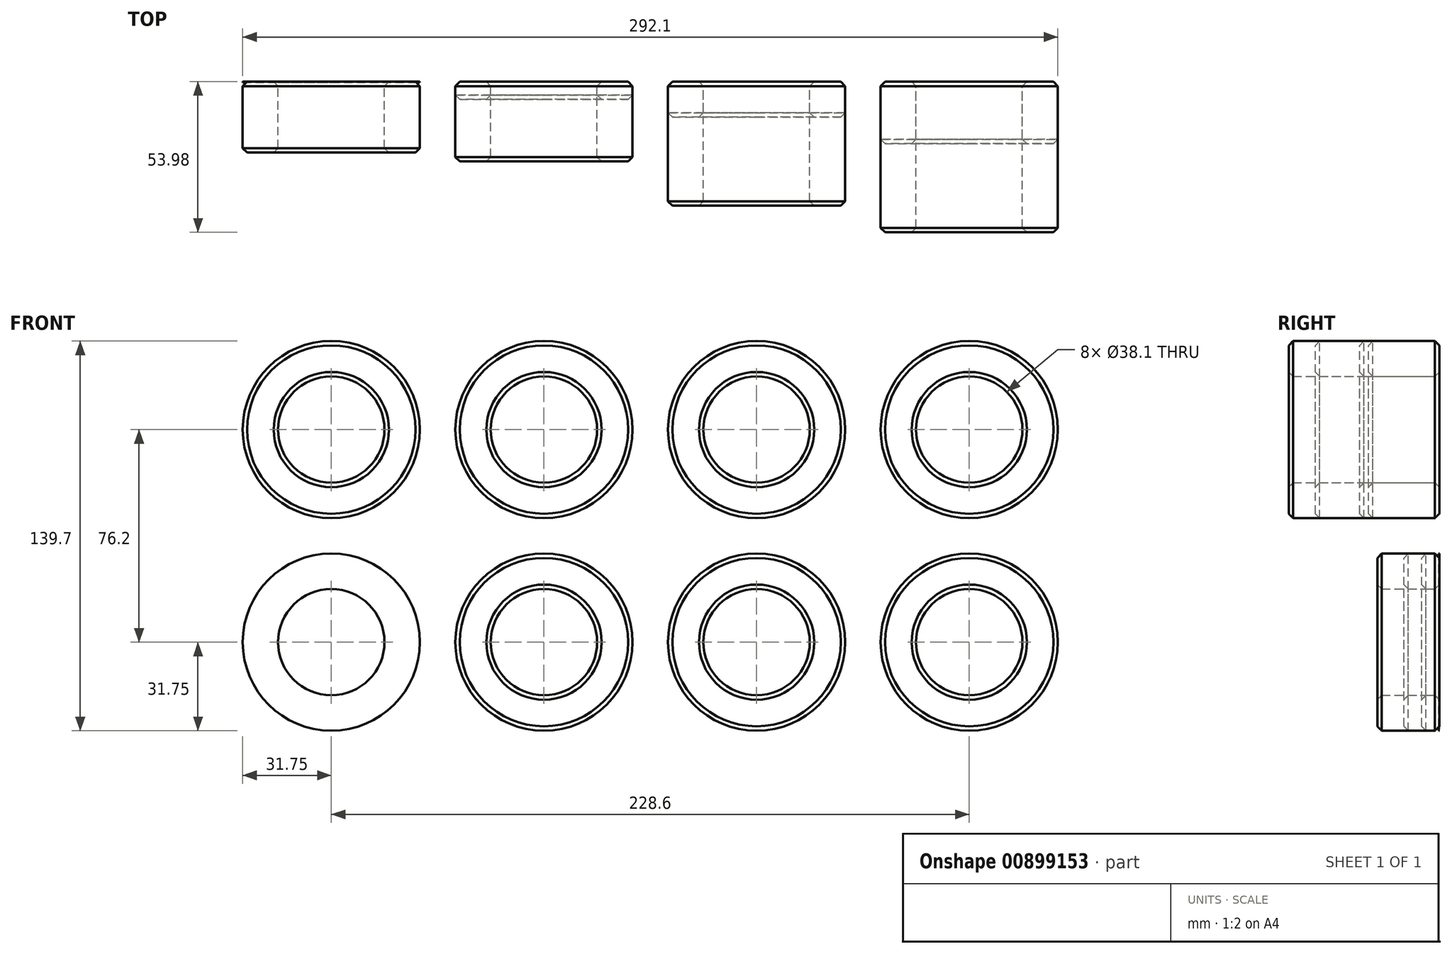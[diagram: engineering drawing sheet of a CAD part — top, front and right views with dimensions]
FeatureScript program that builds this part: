
annotation { "Feature Type Name" : "Feature", "Feature Type Description" : "" }
export const myFeature = defineFeature(function(context is Context, id is Id, definition is map)
    precondition{}
    {
        {
            var Q0;
            Q0=qCreatedBy(makeId("Front.planeOp"),FACE);
            var sketch = newSketch(context, id + "F0", { "sketchPlane" : qUnion([Q0])});
            skCircle(sketch, "E0", {"center": v(0, 0) * mm, "radius": 31.75 * mm});
            skCircle(sketch, "E1", {"center": v(0, 0) * mm, "radius": 19.05 * mm});
            skCircle(sketch, "E2.0.1.0", {"center": v(0, 76.2) * mm, "radius": 31.75 * mm});
            skCircle(sketch, "E2.0.1.1", {"center": v(0, 76.2) * mm, "radius": 19.05 * mm});
            skCircle(sketch, "E2.1.0.0", {"center": v(76.2, 0) * mm, "radius": 31.75 * mm});
            skCircle(sketch, "E2.1.0.1", {"center": v(76.2, 0) * mm, "radius": 19.05 * mm});
            skCircle(sketch, "E2.1.1.0", {"center": v(76.2, 76.2) * mm, "radius": 31.75 * mm});
            skCircle(sketch, "E2.1.1.1", {"center": v(76.2, 76.2) * mm, "radius": 19.05 * mm});
            skCircle(sketch, "E2.2.0.0", {"center": v(152.4, 0) * mm, "radius": 31.75 * mm});
            skCircle(sketch, "E2.2.0.1", {"center": v(152.4, 0) * mm, "radius": 19.05 * mm});
            skCircle(sketch, "E2.2.1.0", {"center": v(152.4, 76.2) * mm, "radius": 31.75 * mm});
            skCircle(sketch, "E2.2.1.1", {"center": v(152.4, 76.2) * mm, "radius": 19.05 * mm});
            skCircle(sketch, "E2.3.0.0", {"center": v(228.6, 0) * mm, "radius": 31.75 * mm});
            skCircle(sketch, "E2.3.0.1", {"center": v(228.6, 0) * mm, "radius": 19.05 * mm});
            skCircle(sketch, "E2.3.1.0", {"center": v(228.6, 76.2) * mm, "radius": 31.75 * mm});
            skCircle(sketch, "E2.3.1.1", {"center": v(228.6, 76.2) * mm, "radius": 19.05 * mm});
            skLineSegment(sketch, "E2.direction1", {"start": v(0, 0) * mm, "end": v(76.2, 0) * mm, "construction": true});
            skLineSegment(sketch, "E2.direction2", {"start": v(0, 0) * mm, "end": v(0, 76.2) * mm, "construction": true});
            skSolve(sketch);
        }
        {
            var Q0;
            Q0=makeQuery(id+"F0.imprint","IMPRINT",FACE,{"disambiguationData":[TD([[makeQuery(id+"F0.imprint","IMPRINT",EDGE,{"derivedFrom":sQuery(id+"F0.wireOp",EDGE,"E0")}),1.0]])]});
            extrude(context, id + "F1", {"entities" : qUnion([Q0]), "depth" : 0.25 * mm, "offsetDistance" : 25.4 * mm});
        }
        {
            var Q0;
            Q0=makeQuery(id+"F0.imprint","IMPRINT",FACE,{"disambiguationData":[TD([[makeQuery(id+"F0.imprint","IMPRINT",EDGE,{"derivedFrom":sQuery(id+"F0.wireOp",EDGE,"E2.1.0.0")}),1.0]])]});
            extrude(context, id + "F2", {"entities" : qUnion([Q0]), "depth" : 6.35 * mm, "offsetDistance" : 25.4 * mm});
        }
        {
            var Q0;
            Q0=makeQuery(id+"F0.imprint","IMPRINT",FACE,{"disambiguationData":[TD([[makeQuery(id+"F0.imprint","IMPRINT",EDGE,{"derivedFrom":sQuery(id+"F0.wireOp",EDGE,"E2.2.0.0")}),1.0]])]});
            extrude(context, id + "F3", {"entities" : qUnion([Q0]), "depth" : 12.7 * mm, "offsetDistance" : 25.4 * mm});
        }
        {
            var Q0;
            Q0=makeQuery(id+"F0.imprint","IMPRINT",FACE,{"disambiguationData":[TD([[makeQuery(id+"F0.imprint","IMPRINT",EDGE,{"derivedFrom":sQuery(id+"F0.wireOp",EDGE,"E2.3.0.0")}),1.0]])]});
            extrude(context, id + "F4", {"entities" : qUnion([Q0]), "depth" : 22.22 * mm, "offsetDistance" : 25.4 * mm});
        }
        {
            var Q0;
            Q0=makeQuery(id+"F0.imprint","IMPRINT",FACE,{"disambiguationData":[TD([[makeQuery(id+"F0.imprint","IMPRINT",EDGE,{"derivedFrom":sQuery(id+"F0.wireOp",EDGE,"E2.0.1.0")}),1.0]])]});
            extrude(context, id + "F5", {"entities" : qUnion([Q0]), "depth" : 25.4 * mm, "offsetDistance" : 25.4 * mm});
        }
        {
            var Q0;
            Q0=makeQuery(id+"F0.imprint","IMPRINT",FACE,{"disambiguationData":[TD([[makeQuery(id+"F0.imprint","IMPRINT",EDGE,{"derivedFrom":sQuery(id+"F0.wireOp",EDGE,"E2.1.1.0")}),1.0]])]});
            extrude(context, id + "F6", {"entities" : qUnion([Q0]), "depth" : 28.57 * mm, "offsetDistance" : 25.4 * mm});
        }
        {
            var Q0;
            Q0=makeQuery(id+"F0.imprint","IMPRINT",FACE,{"disambiguationData":[TD([[makeQuery(id+"F0.imprint","IMPRINT",EDGE,{"derivedFrom":sQuery(id+"F0.wireOp",EDGE,"E2.2.1.0")}),1.0]])]});
            extrude(context, id + "F7", {"entities" : qUnion([Q0]), "depth" : 44.45 * mm, "offsetDistance" : 25.4 * mm});
        }
        {
            var Q0;
            Q0=makeQuery(id+"F0.imprint","IMPRINT",FACE,{"disambiguationData":[TD([[makeQuery(id+"F0.imprint","IMPRINT",EDGE,{"derivedFrom":sQuery(id+"F0.wireOp",EDGE,"E2.3.1.0")}),1.0]])]});
            extrude(context, id + "F8", {"entities" : qUnion([Q0]), "depth" : 53.97 * mm, "offsetDistance" : 25.4 * mm});
        }
        {
            var Q0;
            Q0=makeQuery(id+"F5.opExtrude","CAP_FACE",FACE,{"disambiguationData":[OSD([sQuery(id+"F0.wireOp",EDGE,"E2.0.1.0"),sQuery(id+"F0.wireOp",EDGE,"E2.0.1.1")])],"isStart":false});
            var Q1;
            Q1=makeQuery(id+"F6.opExtrude","CAP_FACE",FACE,{"disambiguationData":[OSD([sQuery(id+"F0.wireOp",EDGE,"E2.1.1.0"),sQuery(id+"F0.wireOp",EDGE,"E2.1.1.1")])],"isStart":false});
            var Q2;
            Q2=makeQuery(id+"F7.opExtrude","CAP_FACE",FACE,{"disambiguationData":[OSD([sQuery(id+"F0.wireOp",EDGE,"E2.2.1.0"),sQuery(id+"F0.wireOp",EDGE,"E2.2.1.1")])],"isStart":false});
            var Q3;
            Q3=makeQuery(id+"F8.opExtrude","CAP_FACE",FACE,{"disambiguationData":[OSD([sQuery(id+"F0.wireOp",EDGE,"E2.3.1.0"),sQuery(id+"F0.wireOp",EDGE,"E2.3.1.1")])],"isStart":false});
            var Q4;
            Q4=makeQuery(id+"F4.opExtrude","CAP_FACE",FACE,{"disambiguationData":[OSD([sQuery(id+"F0.wireOp",EDGE,"E2.3.0.0"),sQuery(id+"F0.wireOp",EDGE,"E2.3.0.1")])],"isStart":false});
            var Q5;
            Q5=makeQuery(id+"F3.opExtrude","CAP_FACE",FACE,{"disambiguationData":[OSD([sQuery(id+"F0.wireOp",EDGE,"E2.2.0.0"),sQuery(id+"F0.wireOp",EDGE,"E2.2.0.1")])],"isStart":false});
            var Q6;
            Q6=makeQuery(id+"F2.opExtrude","CAP_FACE",FACE,{"disambiguationData":[OSD([sQuery(id+"F0.wireOp",EDGE,"E2.1.0.0"),sQuery(id+"F0.wireOp",EDGE,"E2.1.0.1")])],"isStart":false});
            var Q7;
            Q7=makeQuery(id+"F5.opExtrude","CAP_FACE",FACE,{"disambiguationData":[OSD([sQuery(id+"F0.wireOp",EDGE,"E2.0.1.0"),sQuery(id+"F0.wireOp",EDGE,"E2.0.1.1")])],"isStart":true});
            var Q8;
            Q8=makeQuery(id+"F6.opExtrude","CAP_FACE",FACE,{"disambiguationData":[OSD([sQuery(id+"F0.wireOp",EDGE,"E2.1.1.0"),sQuery(id+"F0.wireOp",EDGE,"E2.1.1.1")])],"isStart":true});
            var Q9;
            Q9=makeQuery(id+"F2.opExtrude","CAP_FACE",FACE,{"disambiguationData":[OSD([sQuery(id+"F0.wireOp",EDGE,"E2.1.0.0"),sQuery(id+"F0.wireOp",EDGE,"E2.1.0.1")])],"isStart":true});
            var Q10;
            Q10=makeQuery(id+"F3.opExtrude","CAP_FACE",FACE,{"disambiguationData":[OSD([sQuery(id+"F0.wireOp",EDGE,"E2.2.0.0"),sQuery(id+"F0.wireOp",EDGE,"E2.2.0.1")])],"isStart":true});
            var Q11;
            Q11=makeQuery(id+"F4.opExtrude","CAP_FACE",FACE,{"disambiguationData":[OSD([sQuery(id+"F0.wireOp",EDGE,"E2.3.0.0"),sQuery(id+"F0.wireOp",EDGE,"E2.3.0.1")])],"isStart":true});
            var Q12;
            Q12=makeQuery(id+"F7.opExtrude","CAP_FACE",FACE,{"disambiguationData":[OSD([sQuery(id+"F0.wireOp",EDGE,"E2.2.1.0"),sQuery(id+"F0.wireOp",EDGE,"E2.2.1.1")])],"isStart":true});
            var Q13;
            Q13=makeQuery(id+"F8.opExtrude","CAP_FACE",FACE,{"disambiguationData":[OSD([sQuery(id+"F0.wireOp",EDGE,"E2.3.1.0"),sQuery(id+"F0.wireOp",EDGE,"E2.3.1.1")])],"isStart":true});
            chamfer(context, id + "F9", {"entities" : qUnion([Q0, Q1, Q2, Q3, Q4, Q5, Q6, Q7, Q8, Q9, Q10, Q11, Q12, Q13]), "width" : 1.59 * mm, "tangentPropagation" : true});
        }
    });
